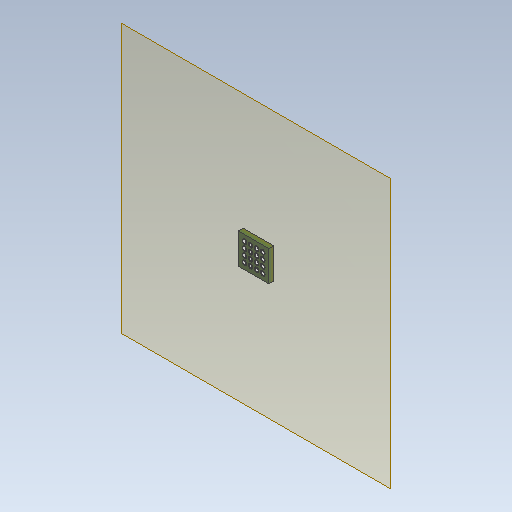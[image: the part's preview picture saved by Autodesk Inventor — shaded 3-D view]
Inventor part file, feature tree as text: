
AUTODESK INVENTOR PART (.ipt)
format: ipt  version: 2021 (Build 250183000, 183)  size: 241,664 bytes
history: native  units: in
note: dims shown in document units (in); Inventor stores cm internally (conversion verified against a paired STEP export)
features: extrude x3, sketch x3, pattern_linear x2, plane x1, mirror x1
ambient origin geometry x8: Origin, YZ Plane, XZ Plane, XY Plane, X Axis, Y Axis, Z Axis, Center Point
bodies: Solid1 (feature_tree)
feature tree (10):
  extrude  "Extrusion1"  Depth=0.25in
  extrude  "Extrusion2"  Depth=0.0394in
  extrude  "Extrusion3"  Depth=0.0006in
  plane  "Work Plane1"
  pattern_linear  "Rectangular Pattern3"  Spacing1=0.0in  [1 undecoded]
  pattern_linear  "Rectangular Pattern4"  Spacing1=0.0394in  [1 undecoded]
  mirror  "Mirror2"
  sketch  "Sketch1"  dims[d0=0.25in d1=0.25in]
  sketch  "Sketch2"  dims[d2=0.0394in d3=0.0in d4=0.0256in]
  sketch  "Sketch3"  dims[d5=0.05in d6=0.05in d7=0.0in d8=0.0in d15=0.0394in d16=0.0006in d17=0.0in d24=1.5748in d26=0.05in d27=1.5748in d29=0.05in d30=1.5748in d32=0.05in d33=1.5748in d35=0.05in]
note: 2 required parameter values undecoded (feature->parameter linkage not recoverable at this tier; creation-order binding heuristic only, values carry confidence <= 0.55)
